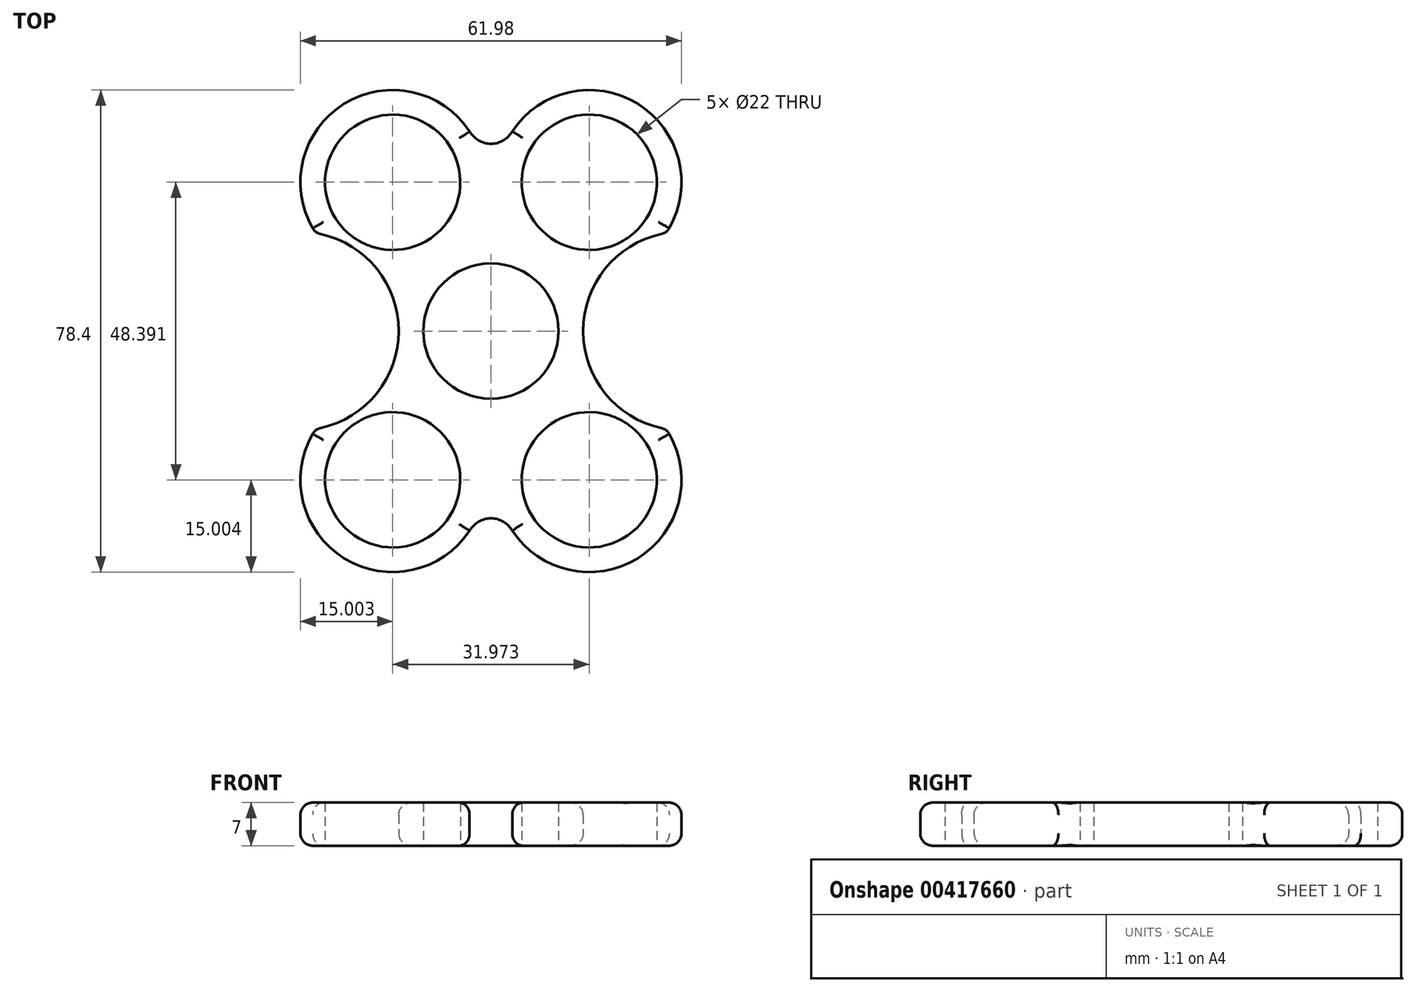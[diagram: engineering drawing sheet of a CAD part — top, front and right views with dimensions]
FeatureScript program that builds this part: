
annotation { "Feature Type Name" : "Feature", "Feature Type Description" : "" }
export const myFeature = defineFeature(function(context is Context, id is Id, definition is map)
    precondition{}
    {
        {
            var Q0;
            Q0=qCreatedBy(makeId("Top.planeOp"),FACE);
            var sketch = newSketch(context, id + "F0", { "sketchPlane" : qUnion([Q0])});
            skCircle(sketch, "E0", {"center": v(0, 0) * mm, "radius": 11 * mm});
            skCircle(sketch, "E1", {"center": v(15.99, 24.2) * mm, "radius": 11 * mm});
            skCircle(sketch, "E2.MirrorC", {"center": v(-15.99, 24.2) * mm, "radius": 11 * mm});
            skCircle(sketch, "E3.MirrorC", {"center": v(-15.99, -24.2) * mm, "radius": 11 * mm});
            skCircle(sketch, "E4.MirrorC", {"center": v(15.99, -24.2) * mm, "radius": 11 * mm});
            skLineSegment(sketch, "E5", {"start": v(0, 0) * mm, "end": v(-15, 0) * mm});
            skLineSegment(sketch, "E6", {"start": v(0, 0) * mm, "end": v(15, 0) * mm});
            skLineSegment(sketch, "E7", {"start": v(-28.5, -15.93) * mm, "end": v(-28.5, -15.93) * mm});
            skArc(sketch, "E8", {"start": v(28.5, 15.93) * mm, "mid": v(16.24, 6.22) * mm, "end": v(17.97, -9.33) * mm});
            skArc(sketch, "E9", {"start": v(-3.47, 32.46) * mm, "mid": v(0, 30.46) * mm, "end": v(3.47, 32.46) * mm});
            skArc(sketch, "E10.MirrorCS", {"start": v(-3.47, -32.46) * mm, "mid": v(0, -30.46) * mm, "end": v(3.47, -32.46) * mm});
            skArc(sketch, "E11", {"start": v(17.97, -9.33) * mm, "mid": v(22.57, -13.68) * mm, "end": v(28.5, -15.93) * mm});
            skArc(sketch, "E12", {"start": v(-28.5, 15.93) * mm, "mid": v(-24.26, 36.71) * mm, "end": v(-3.47, 32.46) * mm});
            skArc(sketch, "E13", {"start": v(-28.5, -15.93) * mm, "mid": v(-15, 0) * mm, "end": v(-28.5, 15.93) * mm});
            skArc(sketch, "E14", {"start": v(28.5, 15.93) * mm, "mid": v(24.1, 36.81) * mm, "end": v(3.27, 32.15) * mm});
            skArc(sketch, "E15", {"start": v(28.5, -15.93) * mm, "mid": v(24.1, -36.81) * mm, "end": v(3.27, -32.15) * mm});
            skArc(sketch, "E16", {"start": v(-28.5, -15.93) * mm, "mid": v(-24.26, -36.71) * mm, "end": v(-3.47, -32.46) * mm});
            skSolve(sketch);
        }
        {
            var Q0;
            Q0=makeQuery(id+"F0.imprint","IMPRINT",FACE,{"disambiguationData":[TD([[makeQuery(id+"F0.imprint","IMPRINT",EDGE,{"derivedFrom":sQuery(id+"F0.wireOp",EDGE,"E1")}),-1.0]])]});
            var Q1;
            Q1=makeQuery(id+"F0.imprint","IMPRINT",FACE,{"disambiguationData":[TD([[makeQuery(id+"F0.imprint","IMPRINT",EDGE,{"derivedFrom":sQuery(id+"F0.wireOp",EDGE,"E3.MirrorC")}),-1.0]])]});
            extrude(context, id + "F1", {"entities" : qUnion([Q0, Q1]), "endBound" : BoundingType.SYMMETRIC, "depth" : 7 * mm});
        }
        {
            var Q0;
            Q0=makeQuery(id+"F1.opExtrude","CAP_EDGE",EDGE,{"disambiguationData":[OSD([sQuery(id+"F0.wireOp",EDGE,"E16")])],"isStart":false});
            var Q1;
            Q1=makeQuery(id+"F1.opExtrude","CAP_EDGE",EDGE,{"disambiguationData":[OSD([sQuery(id+"F0.wireOp",EDGE,"E12")])],"isStart":false});
            var Q2;
            Q2=makeQuery(id+"F1.opExtrude","CAP_EDGE",EDGE,{"disambiguationData":[OSD([sQuery(id+"F0.wireOp",EDGE,"E12")])],"isStart":true});
            var Q3;
            Q3=makeQuery(id+"F1.opExtrude","CAP_EDGE",EDGE,{"disambiguationData":[OSD([sQuery(id+"F0.wireOp",EDGE,"E16")])],"isStart":true});
            var Q4;
            Q4=makeQuery(id+"F1.opExtrude","CAP_EDGE",EDGE,{"disambiguationData":[OSD([sQuery(id+"F0.wireOp",EDGE,"E14")])],"isStart":true});
            var Q5;
            Q5=makeQuery(id+"F1.opExtrude","CAP_EDGE",EDGE,{"disambiguationData":[OSD([sQuery(id+"F0.wireOp",EDGE,"E14")])],"isStart":false});
            var Q6;
            Q6=makeQuery(id+"F1.opExtrude","CAP_EDGE",EDGE,{"disambiguationData":[OSD([sQuery(id+"F0.wireOp",EDGE,"E15")])],"isStart":false});
            var Q7;
            Q7=makeQuery(id+"F1.opExtrude","CAP_EDGE",EDGE,{"disambiguationData":[OSD([sQuery(id+"F0.wireOp",EDGE,"E15")])],"isStart":true});
            fillet(context, id + "F2", {"entities" : qUnion([Q0, Q1, Q2, Q3, Q4, Q5, Q6, Q7]), "radius" : 2 * mm, "tangentPropagation" : true, "allowEdgeOverflow" : false});
        }
        {
            var Q0;
            Q0=makeQuery(id+"F1.opExtrude","CAP_EDGE",EDGE,{"disambiguationData":[OSD([sQuery(id+"F0.wireOp",EDGE,"E13")])],"isStart":false});
            var Q1;
            Q1=makeQuery(id+"F1.opExtrude","CAP_EDGE",EDGE,{"disambiguationData":[OSD([sQuery(id+"F0.wireOp",EDGE,"E13")])],"isStart":true});
            var Q2;
            Q2=makeQuery(id+"F1.opExtrude","CAP_EDGE",EDGE,{"disambiguationData":[OSD([sQuery(id+"F0.wireOp",EDGE,"E8"),sQuery(id+"F0.wireOp",EDGE,"E11")])],"isStart":false});
            var Q3;
            Q3=makeQuery(id+"F1.opExtrude","CAP_EDGE",EDGE,{"disambiguationData":[OSD([sQuery(id+"F0.wireOp",EDGE,"E8"),sQuery(id+"F0.wireOp",EDGE,"E11")])],"isStart":true});
            fillet(context, id + "F3", {"entities" : qUnion([Q0, Q1, Q2, Q3]), "radius" : 2 * mm, "tangentPropagation" : true, "allowEdgeOverflow" : false});
        }
    });
